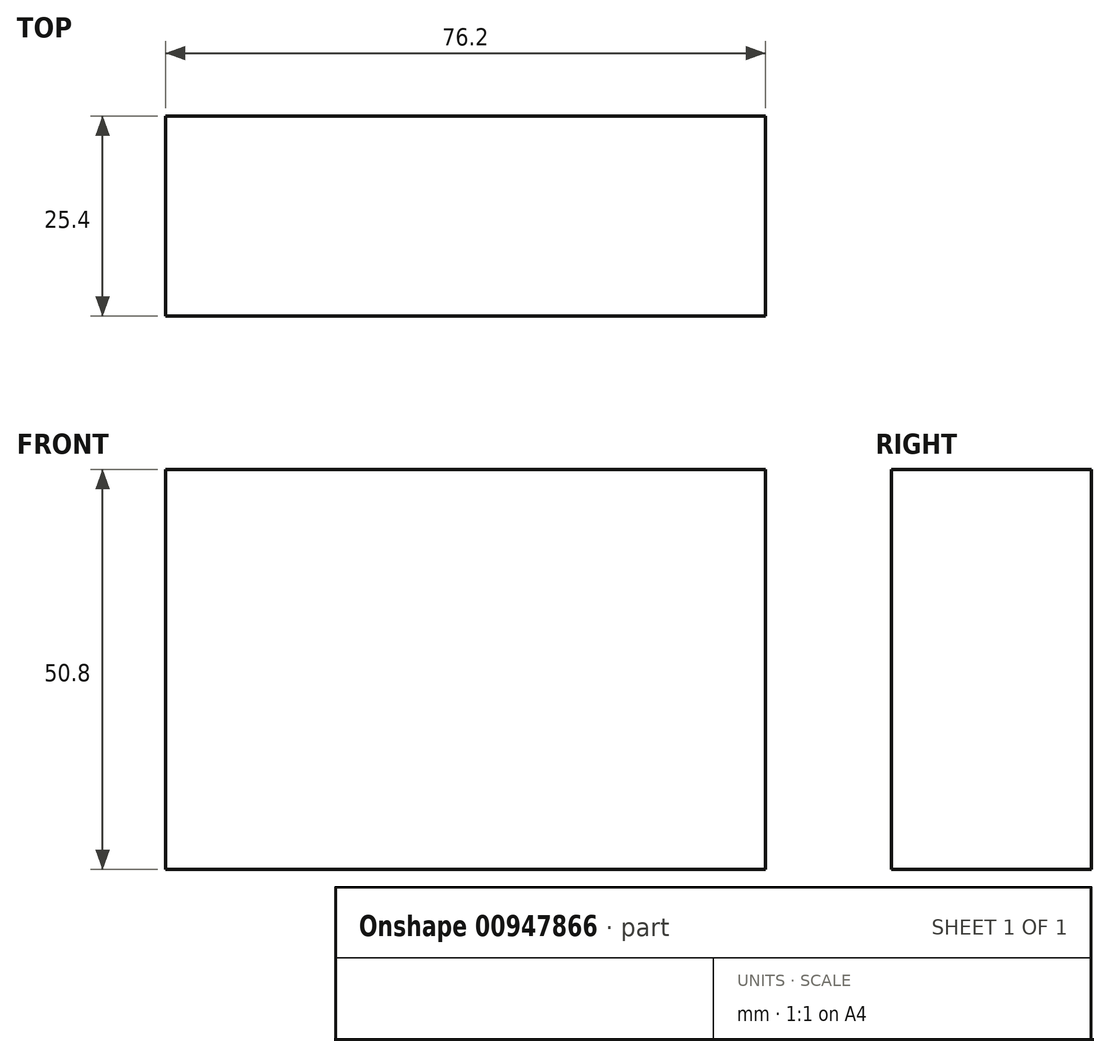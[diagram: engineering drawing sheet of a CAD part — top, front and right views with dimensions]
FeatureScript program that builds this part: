
annotation { "Feature Type Name" : "Feature", "Feature Type Description" : "" }
export const myFeature = defineFeature(function(context is Context, id is Id, definition is map)
    precondition{}
    {
        {
            var Q0;
            Q0=qCreatedBy(makeId("Front.planeOp"),FACE);
            var sketch = newSketch(context, id + "F0", { "sketchPlane" : qUnion([Q0])});
            skLineSegment(sketch, "E0.bottom", {"start": v(38.1, 25.4) * mm, "end": v(-38.1, 25.4) * mm});
            skLineSegment(sketch, "E0.top", {"start": v(38.1, -25.4) * mm, "end": v(-38.1, -25.4) * mm});
            skLineSegment(sketch, "E0.left", {"start": v(38.1, 25.4) * mm, "end": v(38.1, -25.4) * mm});
            skLineSegment(sketch, "E0.right", {"start": v(-38.1, 25.4) * mm, "end": v(-38.1, -25.4) * mm});
            skPoint(sketch, "E0.middle", {"position": v(0, 0) * mm});
            skSolve(sketch);
        }
        {
            var Q0;
            Q0=makeQuery(id+"F0.imprint","IMPRINT",FACE,{"disambiguationData":[TD([[makeQuery(id+"F0.imprint","IMPRINT",EDGE,{"derivedFrom":sQuery(id+"F0.wireOp",EDGE,"E0.bottom")}),1.0]])]});
            extrude(context, id + "F1", {"entities" : qUnion([Q0]), "depth" : 25.4 * mm, "offsetDistance" : 25.4 * mm});
        }
    });
